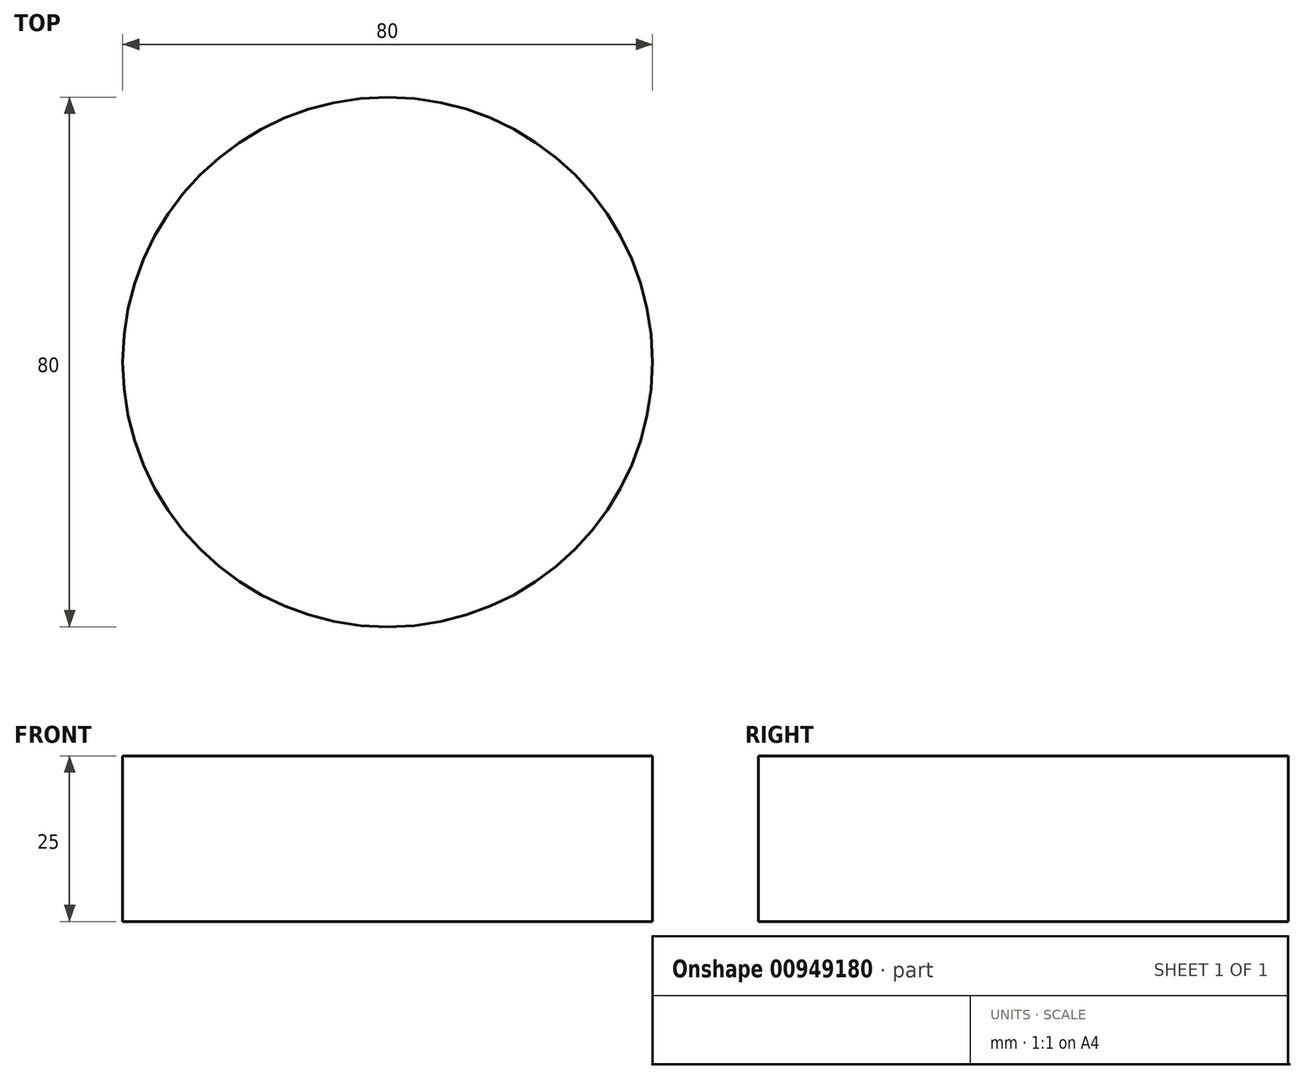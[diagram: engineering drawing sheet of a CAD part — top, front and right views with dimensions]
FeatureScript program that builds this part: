
annotation { "Feature Type Name" : "Feature", "Feature Type Description" : "" }
export const myFeature = defineFeature(function(context is Context, id is Id, definition is map)
    precondition{}
    {
        {
            var Q0;
            Q0=qCreatedBy(makeId("Top.planeOp"),FACE);
            var sketch = newSketch(context, id + "F0", { "sketchPlane" : qUnion([Q0])});
            skCircle(sketch, "E0", {"center": v(0, 0) * mm, "radius": 40 * mm});
            skSolve(sketch);
        }
        {
            var Q0;
            Q0 = qSketchRegion(id + "F0", true);
            extrude(context, id + "F1", {"entities" : qUnion([Q0]), "depth" : 25 * mm, "offsetDistance" : 25 * mm});
        }
    });
